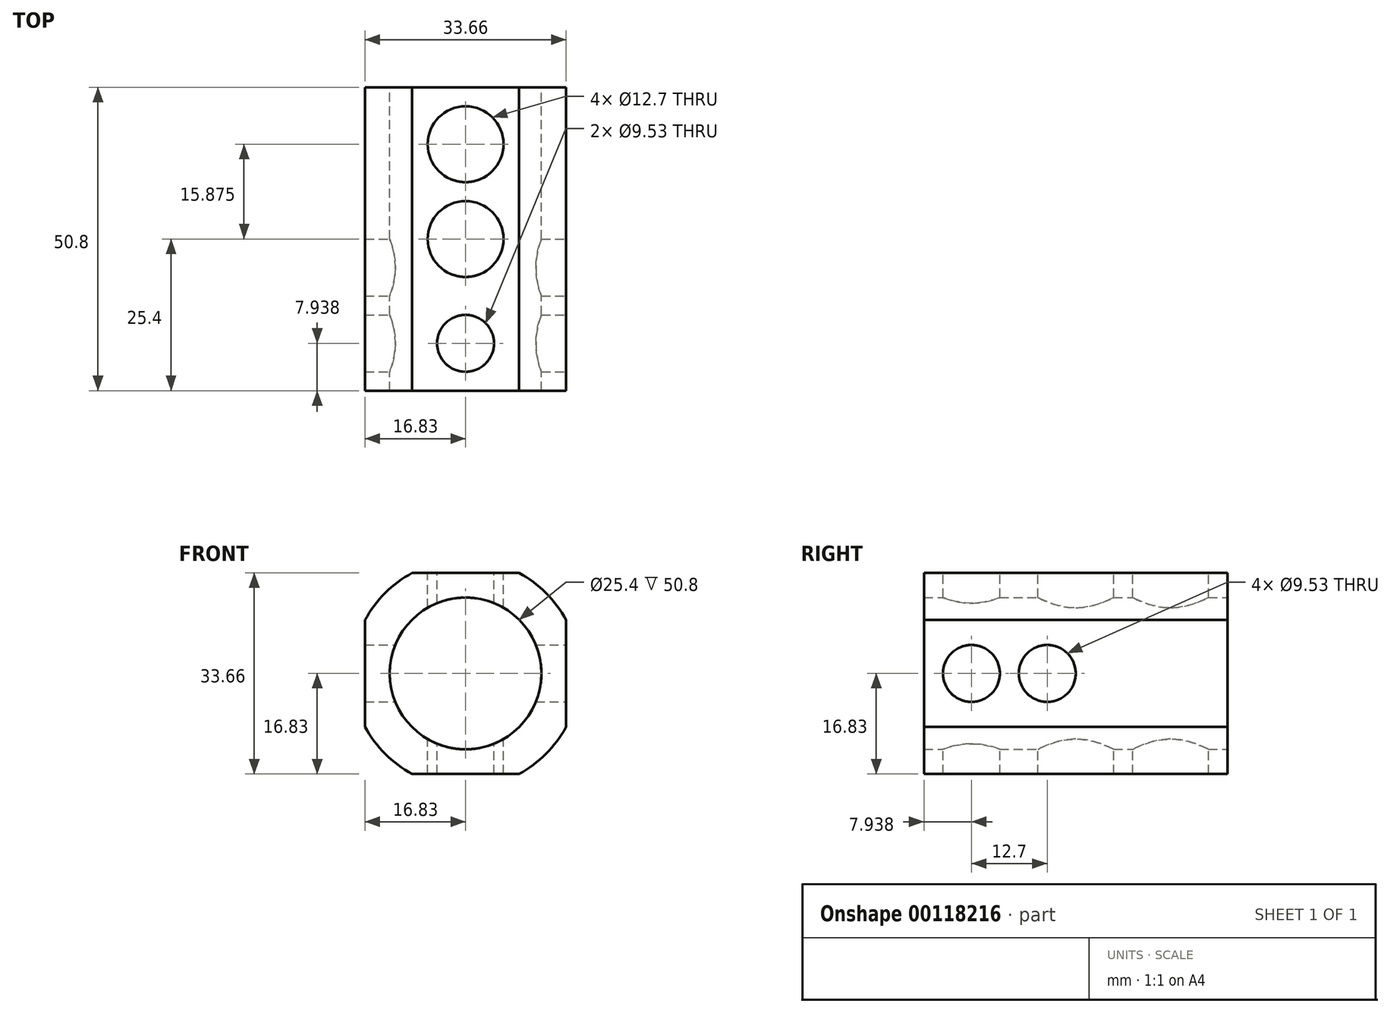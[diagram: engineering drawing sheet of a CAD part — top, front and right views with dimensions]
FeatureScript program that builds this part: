
annotation { "Feature Type Name" : "Feature", "Feature Type Description" : "" }
export const myFeature = defineFeature(function(context is Context, id is Id, definition is map)
    precondition{}
    {
        {
            var Q0;
            Q0=qCreatedBy(makeId("Front.planeOp"),FACE);
            var sketch = newSketch(context, id + "F0", { "sketchPlane" : qUnion([Q0])});
            skArc(sketch, "E0", {"start": v(-8.93, 16.83) * mm, "mid": v(-13.47, 13.47) * mm, "end": v(-16.83, 8.93) * mm});
            skCircle(sketch, "E1", {"center": v(0, 0) * mm, "radius": 12.7 * mm});
            skLineSegment(sketch, "E2.bottom", {"start": v(8.93, 16.83) * mm, "end": v(-8.93, 16.83) * mm});
            skLineSegment(sketch, "E2.top", {"start": v(8.93, -16.83) * mm, "end": v(-8.93, -16.83) * mm});
            skLineSegment(sketch, "E2.left", {"start": v(16.83, 8.93) * mm, "end": v(16.83, -8.93) * mm});
            skLineSegment(sketch, "E2.right", {"start": v(-16.83, 8.93) * mm, "end": v(-16.83, -8.93) * mm});
            skArc(sketch, "E3.trimOffspring", {"start": v(-16.83, -8.93) * mm, "mid": v(-13.47, -13.47) * mm, "end": v(-8.93, -16.83) * mm});
            skArc(sketch, "E4.trimOffspring", {"start": v(16.83, 8.93) * mm, "mid": v(13.47, 13.47) * mm, "end": v(8.93, 16.83) * mm});
            skArc(sketch, "E5.trimOffspring", {"start": v(8.93, -16.83) * mm, "mid": v(13.47, -13.47) * mm, "end": v(16.83, -8.93) * mm});
            skPoint(sketch, "E6.orphan", {"position": v(16.83, -16.83) * mm});
            skPoint(sketch, "E7.orphan", {"position": v(16.83, 16.83) * mm});
            skPoint(sketch, "E8.orphan", {"position": v(-16.83, 16.83) * mm});
            skPoint(sketch, "E9.orphan", {"position": v(-16.83, -16.83) * mm});
            skSolve(sketch);
        }
        {
            var Q0;
            Q0=makeQuery(id+"F0.imprint","IMPRINT",FACE,{"disambiguationData":[TD([[makeQuery(id+"F0.imprint","IMPRINT",EDGE,{"derivedFrom":sQuery(id+"F0.wireOp",EDGE,"E0")}),1.0]])]});
            extrude(context, id + "F1", {"entities" : qUnion([Q0]), "endBound" : BoundingType.SYMMETRIC, "depth" : 50.8 * mm});
        }
        {
            var Q0;
            Q0=makeQuery(id+"F1.opExtrude","SWEPT_FACE",FACE,{"disambiguationData":[OSD([sQuery(id+"F0.wireOp",EDGE,"E2.bottom")])]});
            var sketch = newSketch(context, id + "F2", { "sketchPlane" : qUnion([Q0])});
            skCircle(sketch, "E10", {"center": v(0, 15.88) * mm, "radius": 6.35 * mm});
            skCircle(sketch, "E11", {"center": v(0, 0) * mm, "radius": 6.35 * mm});
            skCircle(sketch, "E12", {"center": v(0, -17.46) * mm, "radius": 4.76 * mm});
            skSolve(sketch);
        }
        {
            var Q0;
            Q0=makeQuery(id+"F1.opExtrude","SWEPT_FACE",FACE,{"disambiguationData":[OSD([sQuery(id+"F0.wireOp",EDGE,"E2.left")])]});
            var sketch = newSketch(context, id + "F3", { "sketchPlane" : qUnion([Q0])});
            skCircle(sketch, "E13", {"center": v(-17.46, 0) * mm, "radius": 4.76 * mm});
            skCircle(sketch, "E14", {"center": v(-4.76, 0) * mm, "radius": 4.76 * mm});
            skSolve(sketch);
        }
        {
            var Q0;
            Q0=sQuery(id+"F2.wireOp",VERTEX,"E10.center");
            var Q1;
            Q1=sQuery(id+"F2.wireOp",VERTEX,"E11.center");
            var Q2;
            Q2=makeQuery(id+"F1.opExtrude","SWEPT_BODY",BODY,{"disambiguationData":[OSD([sQuery(id+"F0.wireOp",EDGE,"E0"),sQuery(id+"F0.wireOp",EDGE,"E1"),sQuery(id+"F0.wireOp",EDGE,"E2.bottom"),sQuery(id+"F0.wireOp",EDGE,"E2.top"),sQuery(id+"F0.wireOp",EDGE,"E2.left"),sQuery(id+"F0.wireOp",EDGE,"E2.right"),sQuery(id+"F0.wireOp",EDGE,"E3.trimOffspring"),sQuery(id+"F0.wireOp",EDGE,"E4.trimOffspring"),sQuery(id+"F0.wireOp",EDGE,"E5.trimOffspring")])]});
            hole(context, id + "F4", {"style" : HoleStyle.SIMPLE, "endStyle" : HoleEndStyle.THROUGH, "holeDiameter" : 12.7 * mm, "startFromSketch" : true, "locations" : qUnion([Q0, Q1]), "scope" : qUnion([Q2]), "isTappedThrough" : true});
        }
        {
            var Q0;
            Q0=sQuery(id+"F2.wireOp",VERTEX,"E12.center");
            var Q1;
            Q1=makeQuery(id+"F1.opExtrude","SWEPT_BODY",BODY,{"disambiguationData":[OSD([sQuery(id+"F0.wireOp",EDGE,"E0"),sQuery(id+"F0.wireOp",EDGE,"E1"),sQuery(id+"F0.wireOp",EDGE,"E2.bottom"),sQuery(id+"F0.wireOp",EDGE,"E2.top"),sQuery(id+"F0.wireOp",EDGE,"E2.left"),sQuery(id+"F0.wireOp",EDGE,"E2.right"),sQuery(id+"F0.wireOp",EDGE,"E3.trimOffspring"),sQuery(id+"F0.wireOp",EDGE,"E4.trimOffspring"),sQuery(id+"F0.wireOp",EDGE,"E5.trimOffspring")])]});
            hole(context, id + "F5", {"style" : HoleStyle.SIMPLE, "endStyle" : HoleEndStyle.THROUGH, "holeDiameter" : 9.52 * mm, "startFromSketch" : true, "locations" : qUnion([Q0]), "scope" : qUnion([Q1]), "isTappedThrough" : true});
        }
        {
            var Q0;
            Q0=sQuery(id+"F3.wireOp",VERTEX,"E14.center");
            var Q1;
            Q1=sQuery(id+"F3.wireOp",VERTEX,"E13.center");
            var Q2;
            Q2=makeQuery(id+"F1.opExtrude","SWEPT_BODY",BODY,{"disambiguationData":[OSD([sQuery(id+"F0.wireOp",EDGE,"E0"),sQuery(id+"F0.wireOp",EDGE,"E1"),sQuery(id+"F0.wireOp",EDGE,"E2.bottom"),sQuery(id+"F0.wireOp",EDGE,"E2.top"),sQuery(id+"F0.wireOp",EDGE,"E2.left"),sQuery(id+"F0.wireOp",EDGE,"E2.right"),sQuery(id+"F0.wireOp",EDGE,"E3.trimOffspring"),sQuery(id+"F0.wireOp",EDGE,"E4.trimOffspring"),sQuery(id+"F0.wireOp",EDGE,"E5.trimOffspring")])]});
            hole(context, id + "F6", {"style" : HoleStyle.SIMPLE, "endStyle" : HoleEndStyle.THROUGH, "holeDiameter" : 9.52 * mm, "startFromSketch" : true, "locations" : qUnion([Q0, Q1]), "scope" : qUnion([Q2]), "isTappedThrough" : true});
        }
    });
